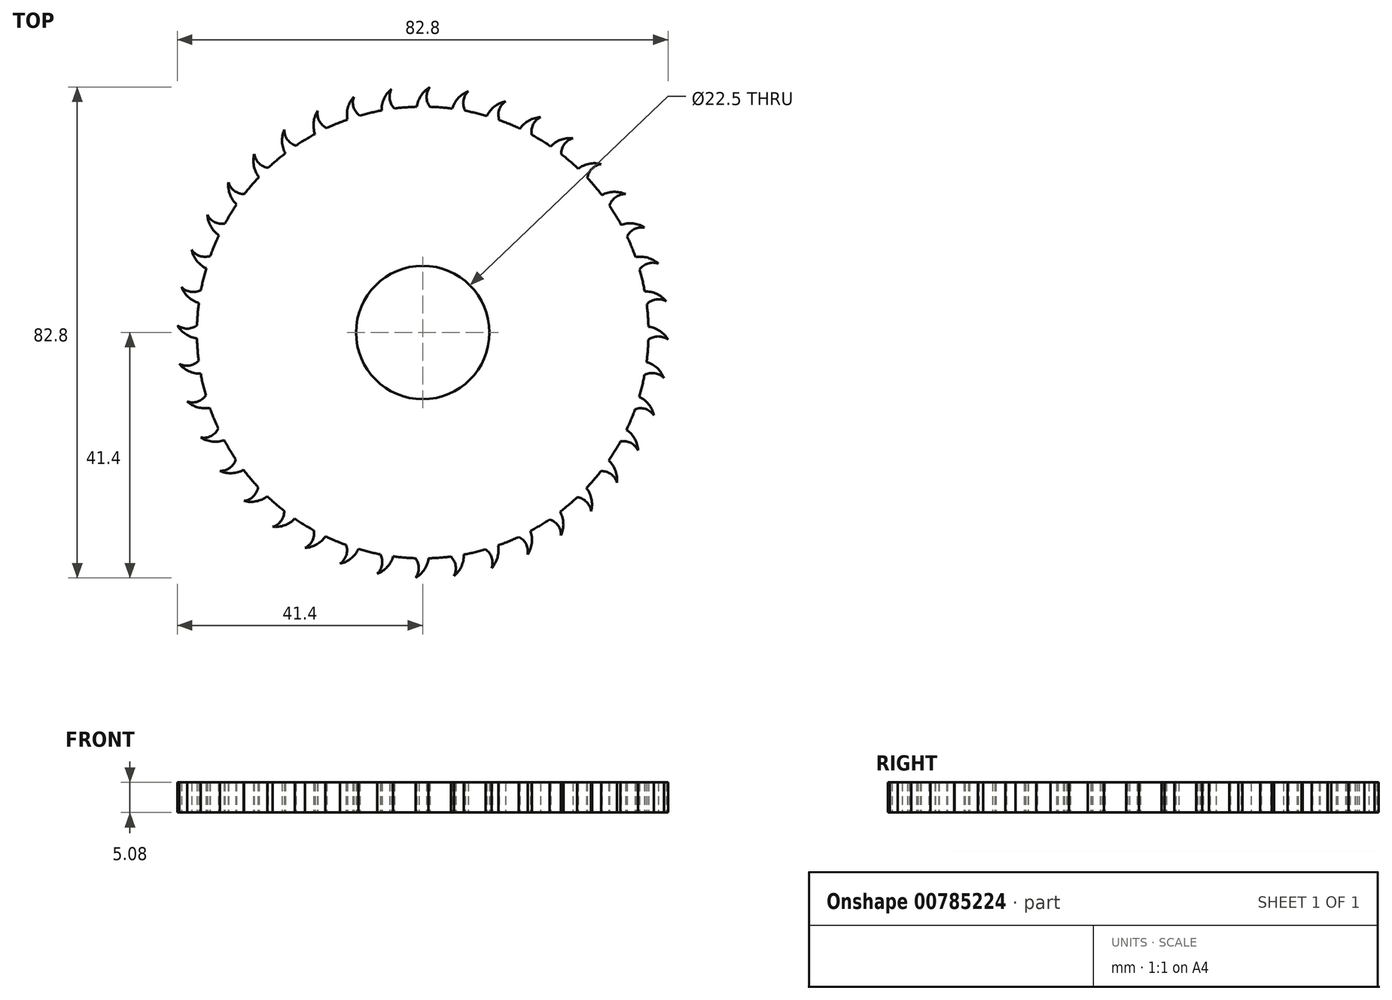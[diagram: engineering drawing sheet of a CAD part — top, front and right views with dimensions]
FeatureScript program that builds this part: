
annotation { "Feature Type Name" : "Feature", "Feature Type Description" : "" }
export const myFeature = defineFeature(function(context is Context, id is Id, definition is map)
    precondition{}
    {
        {
            var Q0;
            Q0=qCreatedBy(makeId("Top.planeOp"),FACE);
            var sketch = newSketch(context, id + "F0", { "sketchPlane" : qUnion([Q0])});
            skCircle(sketch, "E0", {"center": v(0, 0) * mm, "radius": 11.25 * mm});
            skCircle(sketch, "E1", {"center": v(0, 0) * mm, "radius": 38.1 * mm});
            skArc(sketch, "E2", {"start": v(1.22, 41.4) * mm, "mid": v(-0.27, 40) * mm, "end": v(-0.98, 38.09) * mm});
            skArc(sketch, "E3", {"start": v(1.22, 41.4) * mm, "mid": v(0.66, 39.74) * mm, "end": v(1.22, 38.08) * mm});
            skArc(sketch, "E4.1.0", {"start": v(-5.27, 41.08) * mm, "mid": v(-6.52, 39.47) * mm, "end": v(-6.93, 37.46) * mm});
            skArc(sketch, "E4.1.1", {"start": v(-5.27, 41.08) * mm, "mid": v(-5.57, 39.35) * mm, "end": v(-4.75, 37.8) * mm});
            skArc(sketch, "E4.2.0", {"start": v(-11.63, 39.75) * mm, "mid": v(-12.62, 37.96) * mm, "end": v(-12.7, 35.92) * mm});
            skArc(sketch, "E4.2.1", {"start": v(-11.63, 39.75) * mm, "mid": v(-11.66, 38) * mm, "end": v(-10.6, 36.6) * mm});
            skArc(sketch, "E4.3.0", {"start": v(-17.7, 37.44) * mm, "mid": v(-18.4, 35.52) * mm, "end": v(-18.17, 33.49) * mm});
            skArc(sketch, "E4.3.1", {"start": v(-17.7, 37.44) * mm, "mid": v(-17.46, 35.7) * mm, "end": v(-16.2, 34.48) * mm});
            skArc(sketch, "E4.4.0", {"start": v(-23.35, 34.2) * mm, "mid": v(-23.73, 32.2) * mm, "end": v(-23.18, 30.23) * mm});
            skArc(sketch, "E4.4.1", {"start": v(-23.35, 34.2) * mm, "mid": v(-22.83, 32.54) * mm, "end": v(-21.4, 31.52) * mm});
            skArc(sketch, "E4.5.0", {"start": v(-28.4, 30.13) * mm, "mid": v(-28.47, 28.1) * mm, "end": v(-27.63, 26.24) * mm});
            skArc(sketch, "E4.5.1", {"start": v(-28.4, 30.13) * mm, "mid": v(-27.63, 28.56) * mm, "end": v(-26.06, 27.79) * mm});
            skArc(sketch, "E4.6.0", {"start": v(-32.77, 25.32) * mm, "mid": v(-32.52, 23.3) * mm, "end": v(-31.4, 21.6) * mm});
            skArc(sketch, "E4.6.1", {"start": v(-32.77, 25.32) * mm, "mid": v(-31.76, 23.89) * mm, "end": v(-30.1, 23.37) * mm});
            skArc(sketch, "E4.7.0", {"start": v(-36.33, 19.88) * mm, "mid": v(-35.76, 17.92) * mm, "end": v(-34.38, 16.41) * mm});
            skArc(sketch, "E4.7.1", {"start": v(-36.33, 19.88) * mm, "mid": v(-35.1, 18.63) * mm, "end": v(-33.38, 18.38) * mm});
            skArc(sketch, "E4.8.0", {"start": v(-39, 13.95) * mm, "mid": v(-38.12, 12.1) * mm, "end": v(-36.53, 10.83) * mm});
            skArc(sketch, "E4.8.1", {"start": v(-39, 13.95) * mm, "mid": v(-37.6, 12.9) * mm, "end": v(-35.84, 12.93) * mm});
            skArc(sketch, "E4.9.0", {"start": v(-40.7, 7.68) * mm, "mid": v(-39.55, 6) * mm, "end": v(-37.77, 4.99) * mm});
            skArc(sketch, "E4.9.1", {"start": v(-40.7, 7.68) * mm, "mid": v(-39.15, 6.87) * mm, "end": v(-37.42, 7.16) * mm});
            skArc(sketch, "E4.10.0", {"start": v(-41.4, 1.22) * mm, "mid": v(-40, -0.27) * mm, "end": v(-38.09, -0.98) * mm});
            skArc(sketch, "E4.10.1", {"start": v(-41.4, 1.22) * mm, "mid": v(-39.74, 0.66) * mm, "end": v(-38.08, 1.22) * mm});
            skArc(sketch, "E4.11.0", {"start": v(-41.08, -5.27) * mm, "mid": v(-39.47, -6.52) * mm, "end": v(-37.46, -6.93) * mm});
            skArc(sketch, "E4.11.1", {"start": v(-41.08, -5.27) * mm, "mid": v(-39.35, -5.57) * mm, "end": v(-37.8, -4.75) * mm});
            skArc(sketch, "E4.12.0", {"start": v(-39.75, -11.63) * mm, "mid": v(-37.96, -12.62) * mm, "end": v(-35.92, -12.7) * mm});
            skArc(sketch, "E4.12.1", {"start": v(-39.75, -11.63) * mm, "mid": v(-38, -11.66) * mm, "end": v(-36.6, -10.6) * mm});
            skArc(sketch, "E4.13.0", {"start": v(-37.44, -17.7) * mm, "mid": v(-35.52, -18.4) * mm, "end": v(-33.49, -18.17) * mm});
            skArc(sketch, "E4.13.1", {"start": v(-37.44, -17.7) * mm, "mid": v(-35.7, -17.46) * mm, "end": v(-34.48, -16.2) * mm});
            skArc(sketch, "E4.14.0", {"start": v(-34.2, -23.35) * mm, "mid": v(-32.2, -23.73) * mm, "end": v(-30.23, -23.18) * mm});
            skArc(sketch, "E4.14.1", {"start": v(-34.2, -23.35) * mm, "mid": v(-32.54, -22.83) * mm, "end": v(-31.52, -21.4) * mm});
            skArc(sketch, "E4.15.0", {"start": v(-30.13, -28.4) * mm, "mid": v(-28.1, -28.47) * mm, "end": v(-26.24, -27.63) * mm});
            skArc(sketch, "E4.15.1", {"start": v(-30.13, -28.4) * mm, "mid": v(-28.56, -27.63) * mm, "end": v(-27.79, -26.06) * mm});
            skArc(sketch, "E4.16.0", {"start": v(-25.32, -32.77) * mm, "mid": v(-23.3, -32.52) * mm, "end": v(-21.6, -31.4) * mm});
            skArc(sketch, "E4.16.1", {"start": v(-25.32, -32.77) * mm, "mid": v(-23.89, -31.76) * mm, "end": v(-23.37, -30.1) * mm});
            skArc(sketch, "E4.17.0", {"start": v(-19.88, -36.33) * mm, "mid": v(-17.92, -35.76) * mm, "end": v(-16.41, -34.38) * mm});
            skArc(sketch, "E4.17.1", {"start": v(-19.88, -36.33) * mm, "mid": v(-18.63, -35.1) * mm, "end": v(-18.38, -33.38) * mm});
            skArc(sketch, "E4.18.0", {"start": v(-13.95, -39) * mm, "mid": v(-12.1, -38.12) * mm, "end": v(-10.83, -36.53) * mm});
            skArc(sketch, "E4.18.1", {"start": v(-13.95, -39) * mm, "mid": v(-12.9, -37.6) * mm, "end": v(-12.93, -35.84) * mm});
            skArc(sketch, "E4.19.0", {"start": v(-7.68, -40.7) * mm, "mid": v(-6, -39.55) * mm, "end": v(-4.99, -37.77) * mm});
            skArc(sketch, "E4.19.1", {"start": v(-7.68, -40.7) * mm, "mid": v(-6.87, -39.15) * mm, "end": v(-7.16, -37.42) * mm});
            skArc(sketch, "E4.20.0", {"start": v(-1.22, -41.4) * mm, "mid": v(0.27, -40) * mm, "end": v(0.98, -38.09) * mm});
            skArc(sketch, "E4.20.1", {"start": v(-1.22, -41.4) * mm, "mid": v(-0.66, -39.74) * mm, "end": v(-1.22, -38.08) * mm});
            skArc(sketch, "E4.21.0", {"start": v(5.27, -41.08) * mm, "mid": v(6.52, -39.47) * mm, "end": v(6.93, -37.46) * mm});
            skArc(sketch, "E4.21.1", {"start": v(5.27, -41.08) * mm, "mid": v(5.57, -39.35) * mm, "end": v(4.75, -37.8) * mm});
            skArc(sketch, "E4.22.0", {"start": v(11.63, -39.75) * mm, "mid": v(12.62, -37.96) * mm, "end": v(12.7, -35.92) * mm});
            skArc(sketch, "E4.22.1", {"start": v(11.63, -39.75) * mm, "mid": v(11.66, -38) * mm, "end": v(10.6, -36.6) * mm});
            skArc(sketch, "E4.23.0", {"start": v(17.7, -37.44) * mm, "mid": v(18.4, -35.52) * mm, "end": v(18.17, -33.49) * mm});
            skArc(sketch, "E4.23.1", {"start": v(17.7, -37.44) * mm, "mid": v(17.46, -35.7) * mm, "end": v(16.2, -34.48) * mm});
            skArc(sketch, "E4.24.0", {"start": v(23.35, -34.2) * mm, "mid": v(23.73, -32.2) * mm, "end": v(23.18, -30.23) * mm});
            skArc(sketch, "E4.24.1", {"start": v(23.35, -34.2) * mm, "mid": v(22.83, -32.54) * mm, "end": v(21.4, -31.52) * mm});
            skArc(sketch, "E4.25.0", {"start": v(28.4, -30.13) * mm, "mid": v(28.47, -28.1) * mm, "end": v(27.63, -26.24) * mm});
            skArc(sketch, "E4.25.1", {"start": v(28.4, -30.13) * mm, "mid": v(27.63, -28.56) * mm, "end": v(26.06, -27.79) * mm});
            skArc(sketch, "E4.26.0", {"start": v(32.77, -25.32) * mm, "mid": v(32.52, -23.3) * mm, "end": v(31.4, -21.6) * mm});
            skArc(sketch, "E4.26.1", {"start": v(32.77, -25.32) * mm, "mid": v(31.76, -23.89) * mm, "end": v(30.1, -23.37) * mm});
            skArc(sketch, "E4.27.0", {"start": v(36.33, -19.88) * mm, "mid": v(35.76, -17.92) * mm, "end": v(34.38, -16.41) * mm});
            skArc(sketch, "E4.27.1", {"start": v(36.33, -19.88) * mm, "mid": v(35.1, -18.63) * mm, "end": v(33.38, -18.38) * mm});
            skArc(sketch, "E4.28.0", {"start": v(39, -13.95) * mm, "mid": v(38.12, -12.1) * mm, "end": v(36.53, -10.83) * mm});
            skArc(sketch, "E4.28.1", {"start": v(39, -13.95) * mm, "mid": v(37.6, -12.9) * mm, "end": v(35.84, -12.93) * mm});
            skArc(sketch, "E4.29.0", {"start": v(40.7, -7.68) * mm, "mid": v(39.55, -6) * mm, "end": v(37.77, -4.99) * mm});
            skArc(sketch, "E4.29.1", {"start": v(40.7, -7.68) * mm, "mid": v(39.15, -6.87) * mm, "end": v(37.42, -7.16) * mm});
            skArc(sketch, "E4.30.0", {"start": v(41.4, -1.22) * mm, "mid": v(40, 0.27) * mm, "end": v(38.09, 0.98) * mm});
            skArc(sketch, "E4.30.1", {"start": v(41.4, -1.22) * mm, "mid": v(39.74, -0.66) * mm, "end": v(38.08, -1.22) * mm});
            skArc(sketch, "E4.31.0", {"start": v(41.08, 5.27) * mm, "mid": v(39.47, 6.52) * mm, "end": v(37.46, 6.93) * mm});
            skArc(sketch, "E4.31.1", {"start": v(41.08, 5.27) * mm, "mid": v(39.35, 5.57) * mm, "end": v(37.8, 4.75) * mm});
            skArc(sketch, "E4.32.0", {"start": v(39.75, 11.63) * mm, "mid": v(37.96, 12.62) * mm, "end": v(35.92, 12.7) * mm});
            skArc(sketch, "E4.32.1", {"start": v(39.75, 11.63) * mm, "mid": v(38, 11.66) * mm, "end": v(36.6, 10.6) * mm});
            skArc(sketch, "E4.33.0", {"start": v(37.44, 17.7) * mm, "mid": v(35.52, 18.4) * mm, "end": v(33.49, 18.17) * mm});
            skArc(sketch, "E4.33.1", {"start": v(37.44, 17.7) * mm, "mid": v(35.7, 17.46) * mm, "end": v(34.48, 16.2) * mm});
            skArc(sketch, "E4.34.0", {"start": v(34.2, 23.35) * mm, "mid": v(32.2, 23.73) * mm, "end": v(30.23, 23.18) * mm});
            skArc(sketch, "E4.34.1", {"start": v(34.2, 23.35) * mm, "mid": v(32.54, 22.83) * mm, "end": v(31.52, 21.4) * mm});
            skArc(sketch, "E4.35.0", {"start": v(30.13, 28.4) * mm, "mid": v(28.1, 28.47) * mm, "end": v(26.24, 27.63) * mm});
            skArc(sketch, "E4.35.1", {"start": v(30.13, 28.4) * mm, "mid": v(28.56, 27.63) * mm, "end": v(27.79, 26.06) * mm});
            skArc(sketch, "E4.36.0", {"start": v(25.32, 32.77) * mm, "mid": v(23.3, 32.52) * mm, "end": v(21.6, 31.4) * mm});
            skArc(sketch, "E4.36.1", {"start": v(25.32, 32.77) * mm, "mid": v(23.89, 31.76) * mm, "end": v(23.37, 30.1) * mm});
            skArc(sketch, "E4.37.0", {"start": v(19.88, 36.33) * mm, "mid": v(17.92, 35.76) * mm, "end": v(16.41, 34.38) * mm});
            skArc(sketch, "E4.37.1", {"start": v(19.88, 36.33) * mm, "mid": v(18.63, 35.1) * mm, "end": v(18.38, 33.38) * mm});
            skArc(sketch, "E4.38.0", {"start": v(13.95, 39) * mm, "mid": v(12.1, 38.12) * mm, "end": v(10.83, 36.53) * mm});
            skArc(sketch, "E4.38.1", {"start": v(13.95, 39) * mm, "mid": v(12.9, 37.6) * mm, "end": v(12.93, 35.84) * mm});
            skArc(sketch, "E4.39.0", {"start": v(7.68, 40.7) * mm, "mid": v(6, 39.55) * mm, "end": v(4.99, 37.77) * mm});
            skArc(sketch, "E4.39.1", {"start": v(7.68, 40.7) * mm, "mid": v(6.87, 39.15) * mm, "end": v(7.16, 37.42) * mm});
            skSolve(sketch);
        }
        {
            var Q0;
            Q0 = qSketchRegion(id + "F0", true);
            extrude(context, id + "F1", {"entities" : qUnion([Q0]), "depth" : 5.08 * mm, "offsetDistance" : 25.4 * mm});
        }
    });
